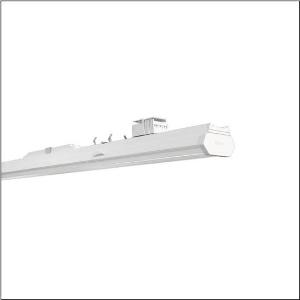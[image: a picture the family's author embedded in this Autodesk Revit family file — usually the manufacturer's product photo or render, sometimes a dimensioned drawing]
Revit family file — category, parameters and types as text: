
# Revit family: licross_r__21_protected_mo_52td1bcn485g_f119
name_source: partatom
category: Lighting Fixtures
units: mm (PartAtom-declared; Revit-internal decimal feet)

## family parameters
Cut with Voids When Loaded = No
Host = Face
Light Source = No
Part Type = Normal
Room Calculation Point = No
Round Connector Dimension = Use Diameter
Shared = No

## types (1)
- --- (1 x LED, 8570 lm, 50.4 W, 4000K)
    Apparent Load = 50 VA
    CIE Flux Codes = 54 82 95 97 100
    Color Rendering = 80
    Color Temperature = 4000K
    Default Elevation = 1800 mm
    Description = Licross® 21 Protected MO, luminaire insert, of sheet steel, galvanised, coil coated, white, length: 1.500mm, width: 90mm, height: 103mm, LED rated luminous flux: 8.570lm, light colour: 840, control gear: ON/OFF Multilumen, CLOi, control gear: ECG Multilumen, with plug, 3-pole, with phase selection, mains connection: 220..240V, AC, 50/60Hz, start of lifetime: 50W, end of service life: 61W, halogen-free wiring, primary optical cover: cover, of PMMA, light emission: direct distribution, primary light characteristic: symmetric, protection rating (complete): IP54, insulation class (complete): insulation class I (protective earthing), certification: CE, ENEC, VDE, UKCA, protection symbol: D if used in an environment with non-conductive dust loads with corresponding accessories, impact resistance: IK06, permissible ambient temperature for indoor applications: -35..+45°C, corresponds to IFS (International Featured Standards) requirements for safety and quality in the food industry, reducing of maximum allowable ambient temperature of 5°C with ceiling mounting, LABS conformity tested according to VDMA 24364:2018-05, packaging unit: 1 piece
    Height = 92 mm
    Lamp = 1 x LED
    Lamp Light Flux = 8570 lm
    Lamp Power = 50.4 W
    Lamp count = 1
    Length = 1500 mm
    Luminous efficacy = 170 lm/W
    Manufacturer = Siteco
    ModVariant = No
    Model = 52TD1BCN485G
    Mounting Place = Ceiling
    Mounting Type = Pendant
    Number of Poles = 1
    OnlyDefault = Yes
    Power Factor = 1
    Product Name = Licross® 21 Protected MO
    Product group = luminaire insert
    ProductGroupID = 901
    Protection Class = Protection class I
    Protection Degree = IP 54
    RLX_Detail_Level = 1
    RLX_Emergency_Light_Flux = 0 lm
    RLX_Emergency_Type = 0
    RLX_Emergency_Type_DB = No
    RlxData = <blob elided: 22081 chars, md5=358c3f35>
    Socket = socket
    Standby Power = 0 W
    System Light Flux = 8570 lm
    System Power = 50 W
    Type Comments = factory setting: luminous flux: 100 % | (A | C | E) | 117 mA
    Type Image = l_1256148.jpg
    URL = http://relux.com
    VarID = @adj_059759
    Voltage = 0 V
    Weight = 0.00 kg
    Width = 88 mm

## geometry (parser evidence)
native form markers: Blend x4, Sweep x9
no freeform markers — native parametric forms only
